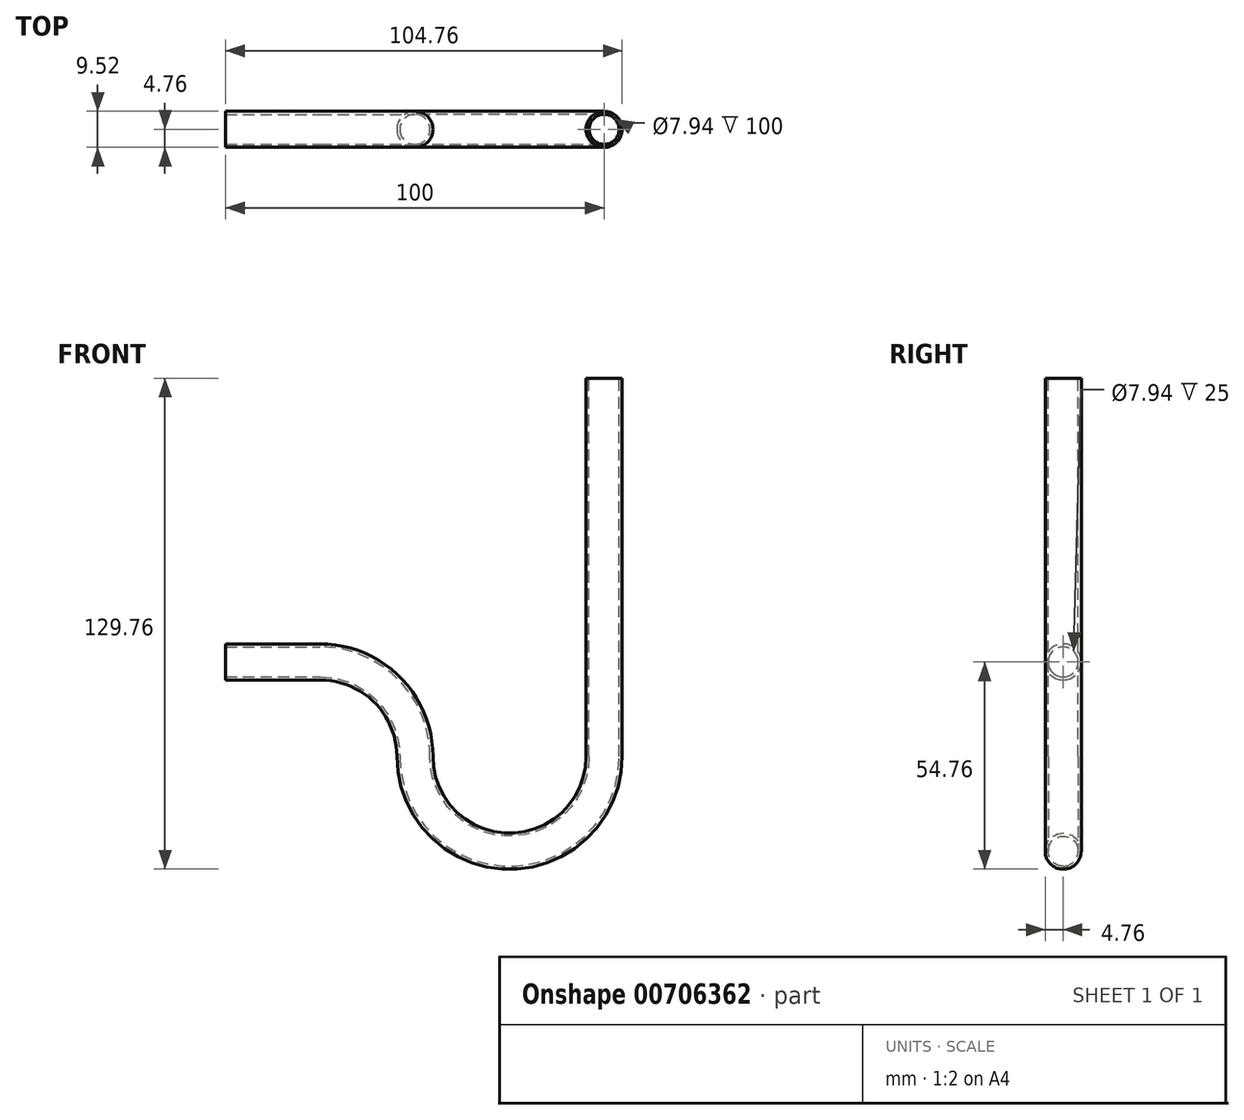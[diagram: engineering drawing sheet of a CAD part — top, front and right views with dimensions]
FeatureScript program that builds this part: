
annotation { "Feature Type Name" : "Feature", "Feature Type Description" : "" }
export const myFeature = defineFeature(function(context is Context, id is Id, definition is map)
    precondition{}
    {
        {
            var Q0;
            Q0=qCreatedBy(makeId("Right.planeOp"),FACE);
            var sketch = newSketch(context, id + "F0", { "sketchPlane" : qUnion([Q0])});
            skCircle(sketch, "E0", {"center": v(0, 0) * mm, "radius": 4.76 * mm});
            skSolve(sketch);
        }
        {
            var Q0;
            Q0=qCreatedBy(makeId("Right.planeOp"),FACE);
            var sketch = newSketch(context, id + "F1", { "sketchPlane" : qUnion([Q0])});
            skCircle(sketch, "E1", {"center": v(0, 0) * mm, "radius": 3.97 * mm});
            skSolve(sketch);
        }
        {
            var Q0;
            Q0=qCreatedBy(makeId("Front.planeOp"),FACE);
            var sketch = newSketch(context, id + "F2", { "sketchPlane" : qUnion([Q0])});
            skLineSegment(sketch, "E2", {"start": v(25, 25) * mm, "end": v(25, 125) * mm});
            skArc(sketch, "E3", {"start": v(-25, 25) * mm, "mid": v(0, 0) * mm, "end": v(25, 25) * mm});
            skArc(sketch, "E4", {"start": v(-25, 25) * mm, "mid": v(-32.32, 42.68) * mm, "end": v(-50, 50) * mm});
            skLineSegment(sketch, "E5", {"start": v(-50, 50) * mm, "end": v(-75, 50) * mm});
            skSolve(sketch);
        }
        {
            var Q0;
            Q0=makeQuery(id+"F0.imprint","IMPRINT",FACE,{"disambiguationData":[TD([[makeQuery(id+"F0.imprint","IMPRINT",EDGE,{"derivedFrom":sQuery(id+"F0.wireOp",EDGE,"E0")}),1.0]])]});
            var Q1;
            Q1=qConstructionFilter(qBodyType(qCreatedBy(id+"F2",EDGE),BodyType.WIRE),ConstructionObject.NO);
            sweep(context, id + "F3", {"profiles" : qUnion([Q0]), "path" : qUnion([Q1])});
        }
        {
            var Q0;
            Q0=makeQuery(id+"F1.imprint","IMPRINT",FACE,{"disambiguationData":[TD([[makeQuery(id+"F1.imprint","IMPRINT",EDGE,{"derivedFrom":sQuery(id+"F1.wireOp",EDGE,"E1")}),1.0]])]});
            var Q1;
            Q1=qConstructionFilter(qBodyType(qCreatedBy(id+"F2",EDGE),BodyType.WIRE),ConstructionObject.NO);
            sweep(context, id + "F4", {"operationType" : NewBodyOperationType.REMOVE, "profiles" : qUnion([Q0]), "path" : qUnion([Q1])});
        }
    });
